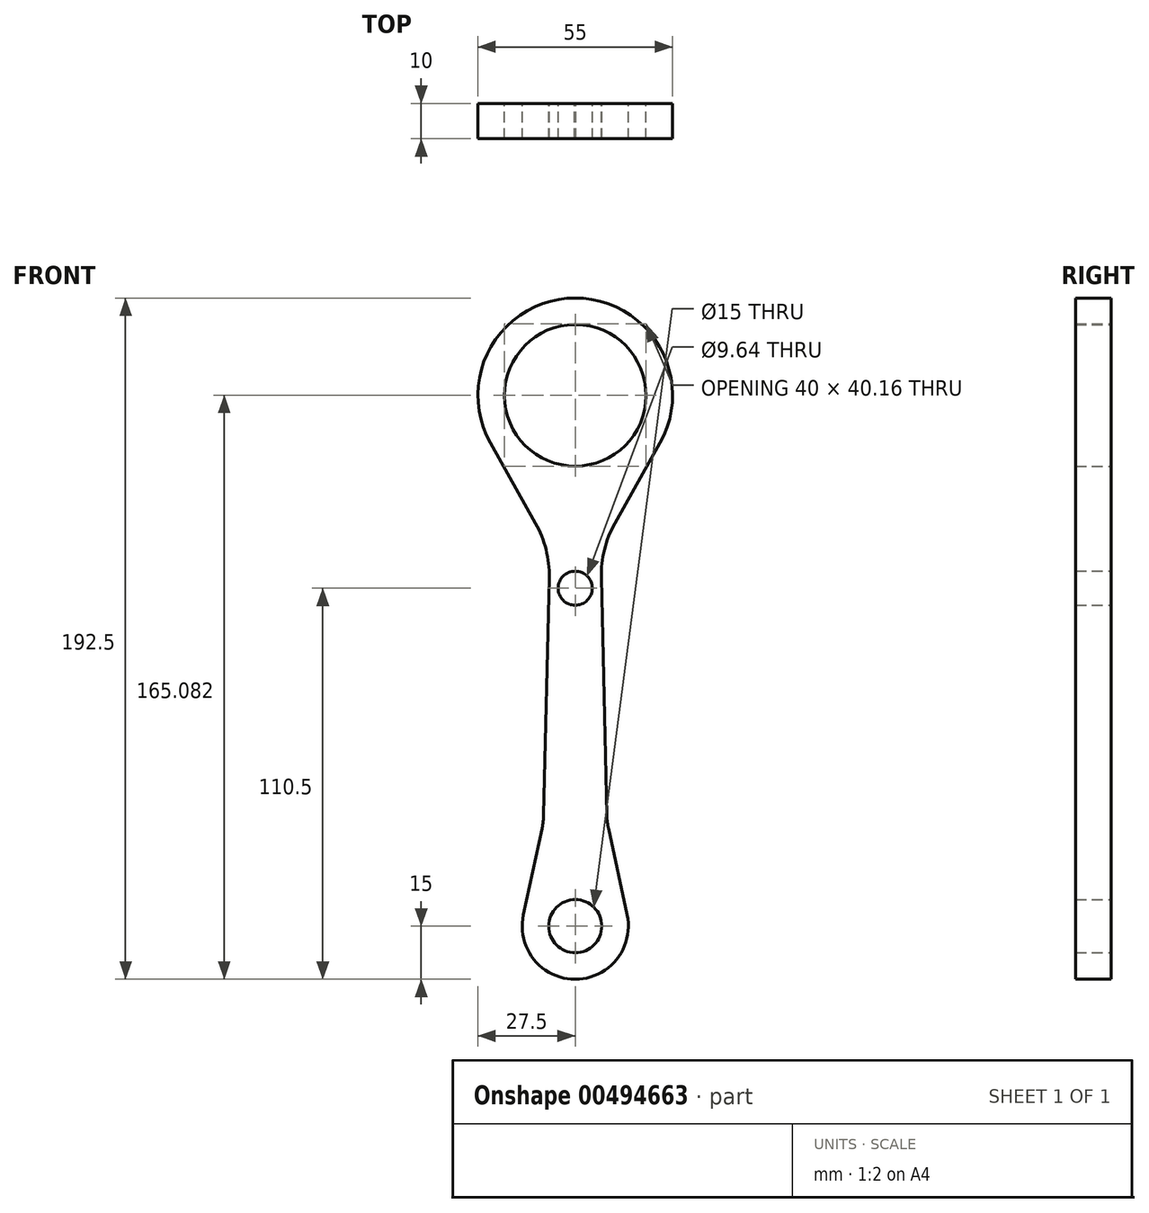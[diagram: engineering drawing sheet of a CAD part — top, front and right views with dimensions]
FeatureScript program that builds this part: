
annotation { "Feature Type Name" : "Feature", "Feature Type Description" : "" }
export const myFeature = defineFeature(function(context is Context, id is Id, definition is map)
    precondition{}
    {
        {
            var Q0;
            Q0=qCreatedBy(makeId("Front.planeOp"),FACE);
            var sketch = newSketch(context, id + "F0", { "sketchPlane" : qUnion([Q0])});
            skArc(sketch, "E0", {"start": v(-0.16, 20) * mm, "mid": v(0, -20) * mm, "end": v(0.16, 20) * mm});
            skArc(sketch, "E1", {"start": v(23.96, -13.5) * mm, "mid": v(0, 27.5) * mm, "end": v(-23.96, -13.5) * mm});
            skCircle(sketch, "E2", {"center": v(0, -150) * mm, "radius": 7.5 * mm});
            skArc(sketch, "E3", {"start": v(-14.66, -146.83) * mm, "mid": v(0, -165) * mm, "end": v(14.66, -146.83) * mm});
            skLineSegment(sketch, "E4", {"start": v(-14.66, -146.83) * mm, "end": v(-9.38, -122.4) * mm});
            skLineSegment(sketch, "E5", {"start": v(-8.94, -118.64) * mm, "end": v(-7.36, -51.57) * mm});
            skLineSegment(sketch, "E6", {"start": v(-11.2, -36.15) * mm, "end": v(-23.96, -13.5) * mm});
            skLineSegment(sketch, "E7.MirrorCS", {"start": v(11.2, -36.15) * mm, "end": v(23.96, -13.5) * mm});
            skLineSegment(sketch, "E8.MirrorCS", {"start": v(8.94, -118.64) * mm, "end": v(7.36, -51.57) * mm});
            skLineSegment(sketch, "E9.MirrorCS", {"start": v(14.66, -146.83) * mm, "end": v(9.38, -122.4) * mm});
            skPoint(sketch, "E10.visualSharp", {"position": v(-7.17, -43.33) * mm});
            skArc(sketch, "E10.filletArc", {"start": v(-7.36, -51.57) * mm, "mid": v(-8.25, -43.6) * mm, "end": v(-11.2, -36.15) * mm});
            skPoint(sketch, "E11.visualSharp", {"position": v(7.17, -43.33) * mm});
            skArc(sketch, "E11.filletArc", {"start": v(11.2, -36.15) * mm, "mid": v(8.25, -43.6) * mm, "end": v(7.36, -51.57) * mm});
            skPoint(sketch, "E12.visualSharp", {"position": v(8.98, -120.54) * mm});
            skArc(sketch, "E12.filletArc", {"start": v(8.94, -118.64) * mm, "mid": v(9.07, -120.53) * mm, "end": v(9.38, -122.4) * mm});
            skPoint(sketch, "E13.visualSharp", {"position": v(-8.98, -120.54) * mm});
            skArc(sketch, "E13.filletArc", {"start": v(-9.38, -122.4) * mm, "mid": v(-9.07, -120.53) * mm, "end": v(-8.94, -118.64) * mm});
            skCircle(sketch, "E14", {"center": v(0, -54.5) * mm, "radius": 4.82 * mm});
            skPoint(sketch, "E15", {"position": v(0, 20) * mm});
            skArc(sketch, "E16", {"start": v(0.16, 20) * mm, "mid": v(0, 20.16) * mm, "end": v(-0.16, 20) * mm});
            skSolve(sketch);
        }
        {
            var Q0;
            Q0 = qSketchRegion(id + "F0", true);
            extrude(context, id + "F1", {"entities" : qUnion([Q0]), "depth" : 10 * mm});
        }
    });
